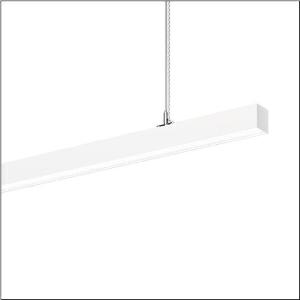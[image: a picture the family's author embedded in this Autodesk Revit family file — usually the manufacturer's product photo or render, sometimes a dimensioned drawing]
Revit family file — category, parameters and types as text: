
# Revit family: silica_r__21_51mx33tbt9w_4d61
name_source: partatom
category: Lighting Fixtures
units: mm (PartAtom-declared; Revit-internal decimal feet)

## family parameters
Cut with Voids When Loaded = No
Host = Face
Light Source = No
Part Type = Normal
Room Calculation Point = No
Round Connector Dimension = Use Diameter
Shared = No

## types (1)
- --- (1 x LED, 7170 lm, 67.4 W, 6500K)
    Apparent Load = 67 VA
    CIE Flux Codes = 78 96 99 56 100
    Color Rendering = 80
    Color Temperature = 6500K
    Default Elevation = 1800 mm
    Description = Silica® 21, office luminaire, primary optical cover: prismatic diffuser, of PMMA, CAT 2 (L<= 3000cd/m²), light emission: direct/indirect distribution, primary light characteristic: symmetric, installation type: suspended mounting, LED, rated luminous flux: 7.170lm, luminous efficacy: 101lm/W, light colour: 8tw, colour temperature: 2700..6500K, control gear: ECG DALI, with terminal, 3+2-pole, max. 2.5mm², mains connection: 220..240V, AC, 50/60Hz, rated input power: 70.8W, luminaire housing, of aluminium, traffic white (RAL 9016), length: 1.504mm, width: 53mm, height: 53mm, protection rating (complete): IP20, insulation class (complete): insulation class I (protective earthing), certification: CE, permissible operating ambient temperature: 0..+35°C, standard: EN 50419, packaging unit: 1 piece
    Height = 53 mm
    Lamp = 1 x LED
    Lamp Light Flux = 7170 lm
    Lamp Power = 67.4 W
    Lamp count = 1
    Length = 1504 mm
    Luminous efficacy = 106 lm/W
    Manufacturer = Siteco
    ModVariant = No
    Model = 51MX33TBT9W
    Mounting Place = Ceiling
    Mounting Type = Pendant
    Number of Poles = 1
    OnlyDefault = Yes
    Power Factor = 1
    Product Name = Silica® 21
    Product group = office luminaire | ceiling pendant
    ProductGroupID = 902
    Protection Class = Protection class I
    Protection Degree = IP 20
    RLX_Detail_Level = 1
    RLX_Emergency_Light_Flux = 0 lm
    RLX_Emergency_Type = 0
    RLX_Emergency_Type_DB = No
    RlxData = <blob elided: 18193 chars, md5=a1b62406>
    Socket = socket
    Standby Power = 0 W
    System Light Flux = 7170 lm
    System Power = 67 W
    Type Comments = individual setting
    Type Image = l_1335916.jpg
    URL = http://relux.com
    VarID = @adj_109579
    Voltage = 0 V
    Weight = 0.00 kg
    Width = 53 mm

## geometry (parser evidence)
native form markers: Blend x4, Sweep x13
no freeform markers — native parametric forms only
